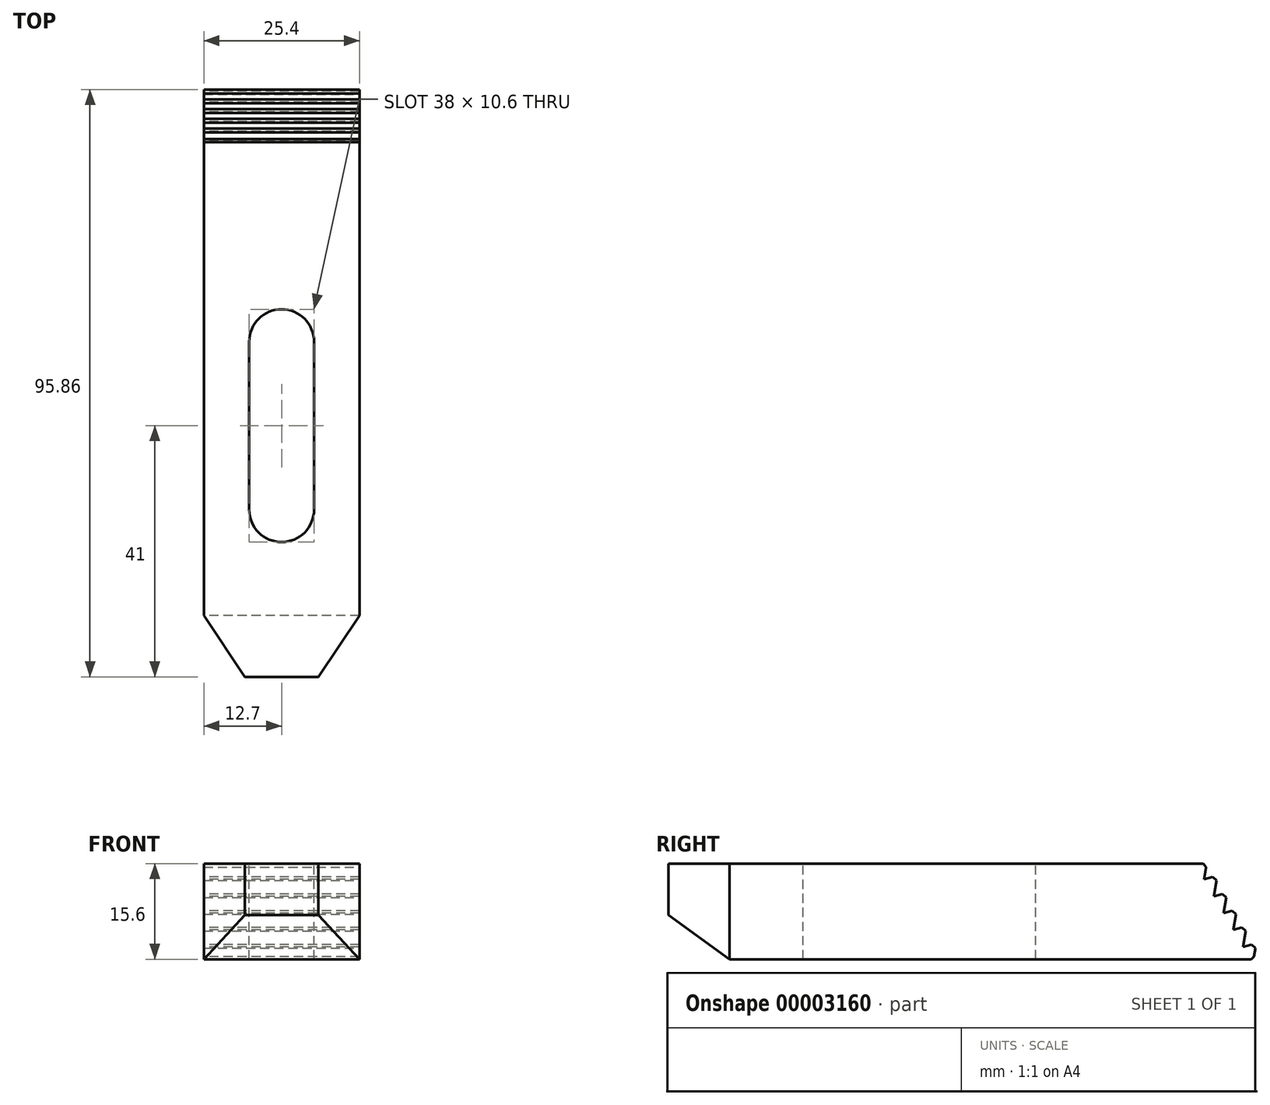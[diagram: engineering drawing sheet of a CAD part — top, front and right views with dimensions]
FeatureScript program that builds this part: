
annotation { "Feature Type Name" : "Feature", "Feature Type Description" : "" }
export const myFeature = defineFeature(function(context is Context, id is Id, definition is map)
    precondition{}
    {
        {
            var Q0;
            Q0=qCreatedBy(makeId("Right.planeOp"),FACE);
            var sketch = newSketch(context, id + "F0", { "sketchPlane" : qUnion([Q0])});
            skLineSegment(sketch, "E0", {"start": v(-31, 0) * mm, "end": v(54.54, 0) * mm});
            skLineSegment(sketch, "E1", {"start": v(54.54, 0) * mm, "end": v(55, 2.6) * mm});
            skLineSegment(sketch, "E2", {"start": v(55, 2.6) * mm, "end": v(52.82, 2.02) * mm});
            skLineSegment(sketch, "E3", {"start": v(52.82, 2.02) * mm, "end": v(53.4, 5.35) * mm});
            skLineSegment(sketch, "E4", {"start": v(53.4, 5.35) * mm, "end": v(51.23, 4.77) * mm});
            skLineSegment(sketch, "E5", {"start": v(51.23, 4.77) * mm, "end": v(51.82, 8.1) * mm});
            skLineSegment(sketch, "E6", {"start": v(51.82, 8.1) * mm, "end": v(49.64, 7.52) * mm});
            skLineSegment(sketch, "E7", {"start": v(49.64, 7.52) * mm, "end": v(50.23, 10.86) * mm});
            skLineSegment(sketch, "E8", {"start": v(50.23, 10.86) * mm, "end": v(48.05, 10.28) * mm});
            skLineSegment(sketch, "E9", {"start": v(48.05, 10.28) * mm, "end": v(48.64, 13.62) * mm});
            skLineSegment(sketch, "E10", {"start": v(48.64, 13.62) * mm, "end": v(46.46, 13.03) * mm});
            skLineSegment(sketch, "E11", {"start": v(46.46, 13.03) * mm, "end": v(46.91, 15.6) * mm});
            skLineSegment(sketch, "E12", {"start": v(46.91, 15.6) * mm, "end": v(-41, 15.6) * mm});
            skLineSegment(sketch, "E13", {"start": v(-41, 15.6) * mm, "end": v(-41, 7.2) * mm});
            skLineSegment(sketch, "E14", {"start": v(-41, 7.2) * mm, "end": v(-31, 0) * mm});
            skLineSegment(sketch, "E15", {"start": v(47.28, 15.98) * mm, "end": v(56.5, 0) * mm, "construction": true});
            skSolve(sketch);
        }
        {
            var Q0;
            Q0 = qSketchRegion(id + "F0", true);
            extrude(context, id + "F1", {"entities" : qUnion([Q0]), "depth" : 25.4 * mm});
        }
        {
            var Q0;
            Q0=makeQuery(id+"F1.opExtrude","SWEPT_FACE",FACE,{"disambiguationData":[OSD([sQuery(id+"F0.wireOp",EDGE,"E12")])]});
            var sketch = newSketch(context, id + "F2", { "sketchPlane" : qUnion([Q0])});
            skLineSegment(sketch, "E16.bottom", {"start": v(18, -13.7) * mm, "end": v(7.4, -13.7) * mm});
            skLineSegment(sketch, "E16.top", {"start": v(18, 13.7) * mm, "end": v(7.4, 13.7) * mm});
            skLineSegment(sketch, "E16.left", {"start": v(18, -13.7) * mm, "end": v(18, 13.7) * mm});
            skLineSegment(sketch, "E16.right", {"start": v(7.4, -13.7) * mm, "end": v(7.4, 13.7) * mm});
            skArc(sketch, "E17", {"start": v(7.4, -13.7) * mm, "mid": v(12.7, -19) * mm, "end": v(18, -13.7) * mm});
            skArc(sketch, "E18", {"start": v(18, 13.7) * mm, "mid": v(12.7, 19) * mm, "end": v(7.4, 13.7) * mm});
            skPoint(sketch, "E19", {"position": v(12.7, -41) * mm});
            skSolve(sketch);
        }
        {
            var Q0;
            Q0 = qSketchRegion(id + "F2", true);
            extrude(context, id + "F3", {"entities" : qUnion([Q0]), "operationType" : NewBodyOperationType.REMOVE, "endBound" : BoundingType.THROUGH_ALL, "oppositeDirection" : true, "depth" : 25 * mm});
        }
        {
            var Q0;
            Q0=makeQuery(id+"F1.opExtrude","SWEPT_FACE",FACE,{"disambiguationData":[OSD([sQuery(id+"F0.wireOp",EDGE,"E12")])]});
            var sketch = newSketch(context, id + "F4", { "sketchPlane" : qUnion([Q0])});
            skLineSegment(sketch, "E20", {"start": v(6.7, -41) * mm, "end": v(0, -31) * mm});
            skArc(sketch, "E21.0", {"start": v(7.4, -13.7) * mm, "mid": v(12.7, -19) * mm, "end": v(18, -13.7) * mm});
            skLineSegment(sketch, "E22", {"start": v(0, -31) * mm, "end": v(0, -41) * mm});
            skLineSegment(sketch, "E23", {"start": v(0, -41) * mm, "end": v(6.7, -41) * mm});
            skLineSegment(sketch, "E24", {"start": v(25.4, -41) * mm, "end": v(25.4, -31) * mm});
            skLineSegment(sketch, "E25", {"start": v(25.4, -31) * mm, "end": v(18.7, -41) * mm});
            skLineSegment(sketch, "E26", {"start": v(18.7, -41) * mm, "end": v(25.4, -41) * mm});
            skSolve(sketch);
        }
        {
            var Q0;
            {var subQ2=sQuery(id+"F4.wireOp",EDGE,"E20");Q0=makeQuery(id+"F4.imprint","IMPRINT",FACE,{"disambiguationData":[TD([[makeQuery(id+"F4.imprint","IMPRINT",EDGE,{"derivedFrom":subQ2}),1.0]])]});}
            var Q1;
            {var subQ2=sQuery(id+"F4.wireOp",EDGE,"67fe6542-2a01-40b1-8eaf-e9a2c91f5f84");Q1=makeQuery(id+"F4.imprint","IMPRINT",FACE,{"disambiguationData":[TD([[makeQuery(id+"F4.imprint","IMPRINT",EDGE,{"derivedFrom":subQ2}),1.0]])]});}
            var Q2;
            {var subQ3=sQuery(id+"F4.wireOp",EDGE,"9a1549f8-947c-4cbd-bb99-a68363a6b833");Q2=makeQuery(id+"F4.imprint","IMPRINT",FACE,{"disambiguationData":[TD([[makeQuery(id+"F4.imprint","IMPRINT",EDGE,{"derivedFrom":subQ3}),1.0]])]});}
            extrude(context, id + "F5", {"entities" : qUnion([Q0, Q1, Q2]), "operationType" : NewBodyOperationType.REMOVE, "endBound" : BoundingType.THROUGH_ALL, "oppositeDirection" : true, "depth" : 25 * mm});
        }
        {
            var Q0;
            Q0 = qSketchRegion(id + "F4", true);
            extrude(context, id + "F6", {"entities" : qUnion([Q0]), "operationType" : NewBodyOperationType.REMOVE, "endBound" : BoundingType.THROUGH_ALL, "oppositeDirection" : true, "depth" : 25 * mm});
        }
        {
            var Q0;
            Q0=makeQuery(id+"F1.opExtrude","SWEPT_EDGE",EDGE,{"disambiguationData":[OSD([sQuery(id+"F0.wireOp",EDGE,"E1"),sQuery(id+"F0.wireOp",EDGE,"E2")])]});
            var Q1;
            Q1=makeQuery(id+"F1.opExtrude","SWEPT_EDGE",EDGE,{"disambiguationData":[OSD([sQuery(id+"F0.wireOp",EDGE,"E3"),sQuery(id+"F0.wireOp",EDGE,"E4")])]});
            var Q2;
            Q2=makeQuery(id+"F1.opExtrude","SWEPT_EDGE",EDGE,{"disambiguationData":[OSD([sQuery(id+"F0.wireOp",EDGE,"E5"),sQuery(id+"F0.wireOp",EDGE,"E6")])]});
            var Q3;
            Q3=makeQuery(id+"F1.opExtrude","SWEPT_EDGE",EDGE,{"disambiguationData":[OSD([sQuery(id+"F0.wireOp",EDGE,"E7"),sQuery(id+"F0.wireOp",EDGE,"E8")])]});
            var Q4;
            Q4=makeQuery(id+"F1.opExtrude","SWEPT_EDGE",EDGE,{"disambiguationData":[OSD([sQuery(id+"F0.wireOp",EDGE,"E9"),sQuery(id+"F0.wireOp",EDGE,"E10")])]});
            var Q5;
            Q5=makeQuery(id+"F1.opExtrude","SWEPT_EDGE",EDGE,{"disambiguationData":[OSD([sQuery(id+"F0.wireOp",EDGE,"E11"),sQuery(id+"F0.wireOp",EDGE,"E12")])]});
            var Q6;
            Q6=makeQuery(id+"F1.opExtrude","SWEPT_EDGE",EDGE,{"disambiguationData":[OSD([sQuery(id+"F0.wireOp",EDGE,"E0"),sQuery(id+"F0.wireOp",EDGE,"E1")])]});
            chamfer(context, id + "F7", {"entities" : qUnion([Q0, Q1, Q2, Q3, Q4, Q5, Q6]), "width" : .5 * mm, "tangentPropagation" : true});
        }
    });
